# Revit family: LAMP_ACC WALL ARM
name_source: partatom
category: Modelos genéricos
revit_build: Autodesk Revit 2015 (Build: 20140606_1530(x64)
units: mm (PartAtom-declared; Revit-internal decimal feet)

## types (4) — shared parameters
Elevación por defecto = 1219 mm
Fabricante = LAMP
Installation instructions = https://www.lamp.es
Last update = 18/08/2020
Manufacturer URL = http://www.lamp.es
Manufacturer country = Spain
Manufacturer name = LAMP
Product URL = https://www.lamp.es
Product datasheet = https://www.lamp.es

## per-type parameters (varying)
| type | Accessory Type | Comentarios de tipo | Descripción | Finish | Material | Model explanation | Modelo | Product code | Weight |
| ADJ & EXT GREY | Adjustable and extensible bracket | Extensible from 280 mm to 380 mm, and tiltable between -90º and 90º. Can be used without extensible part. | ACC. ADJ EXTEN WALL ARM GR. | Textured grey | LAMP_Aluminio genérico | Extensible from 280 mm to 380 mm, and tiltable between -90º and 90º. Can be used without extensible part. | ARROEX40G
ARROEX40G | ARROEX40G
ARROEX40G | 1.67 kg |
| ADJ & EXT WHITE | Adjustable and extensible bracket | Extensible from 280 mm to 380 mm, and tiltable between -90º and 90º. Can be used without extensible part. | ACC. ADJ EXTEN WALL ARM WH. | Shiny white | LAMP_Aluminio genérico blanco | Extensible from 280 mm to 380 mm, and tiltable between -90º and 90º. Can be used without extensible part. | ARROEX40W | ARROEX40W | 1.67 kg |
| ADJ WHITE | Adjustable bracket | Tiltable between -90º and 90º. | ACC. ADJ WALL ARM WH. | Shiny white | LAMP_Aluminio genérico blanco | Tiltable between -90º and 90º. | ARRO13W | ARRO13W | 0.97 kg |
| ADJ GREY | Adjustable bracket | Tiltable between -90º and 90º. | ACC. ADJ WALL ARM GR. | Textured grey | LAMP_Aluminio genérico | Tiltable between -90º and 90º. | ARRO13G | ARRO13G | 0.97 kg |
